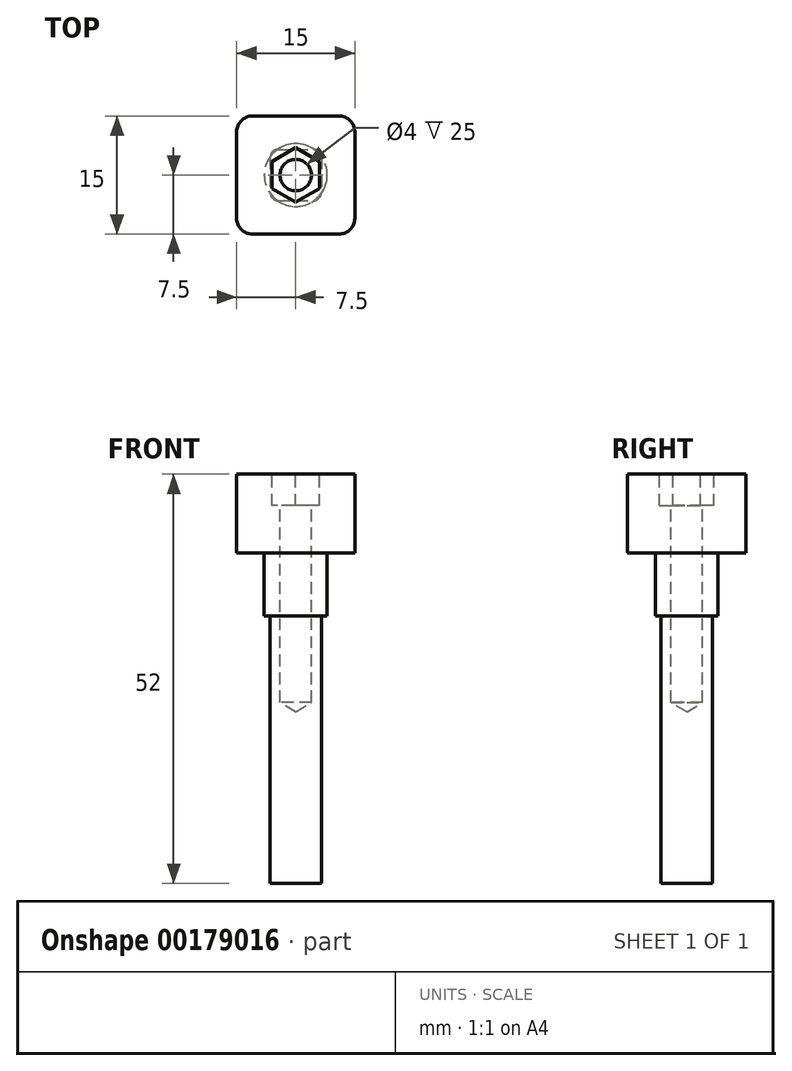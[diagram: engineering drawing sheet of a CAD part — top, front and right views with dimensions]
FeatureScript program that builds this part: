
annotation { "Feature Type Name" : "Feature", "Feature Type Description" : "" }
export const myFeature = defineFeature(function(context is Context, id is Id, definition is map)
    precondition{}
    {
        {
            var Q0;
            Q0=qCreatedBy(makeId("Top.planeOp"),FACE);
            var sketch = newSketch(context, id + "F0", { "sketchPlane" : qUnion([Q0])});
            skLineSegment(sketch, "E0.bottom", {"start": v(-3.25, 3.25) * mm, "end": v(3.25, 3.25) * mm});
            skLineSegment(sketch, "E0.top", {"start": v(-3.25, -3.25) * mm, "end": v(3.25, -3.25) * mm});
            skLineSegment(sketch, "E0.left", {"start": v(-3.25, 3.25) * mm, "end": v(-3.25, -3.25) * mm});
            skLineSegment(sketch, "E0.right", {"start": v(3.25, 3.25) * mm, "end": v(3.25, -3.25) * mm});
            skPoint(sketch, "E0.middle", {"position": v(0, 0) * mm});
            skSolve(sketch);
        }
        {
            var Q0;
            Q0 = qSketchRegion(id + "F0", true);
            extrude(context, id + "F1", {"entities" : qUnion([Q0]), "depth" : 34 * mm});
        }
        {
            var Q0;
            Q0=makeQuery(id+"F1.opExtrude","SWEPT_EDGE",EDGE,{"disambiguationData":[OSD([sQuery(id+"F0.wireOp",EDGE,"E0.bottom"),sQuery(id+"F0.wireOp",EDGE,"E0.left")])]});
            var Q1;
            Q1=makeQuery(id+"F1.opExtrude","SWEPT_EDGE",EDGE,{"disambiguationData":[OSD([sQuery(id+"F0.wireOp",EDGE,"E0.bottom"),sQuery(id+"F0.wireOp",EDGE,"E0.right")])]});
            var Q2;
            Q2=makeQuery(id+"F1.opExtrude","SWEPT_EDGE",EDGE,{"disambiguationData":[OSD([sQuery(id+"F0.wireOp",EDGE,"E0.top"),sQuery(id+"F0.wireOp",EDGE,"E0.right")])]});
            var Q3;
            Q3=makeQuery(id+"F1.opExtrude","SWEPT_EDGE",EDGE,{"disambiguationData":[OSD([sQuery(id+"F0.wireOp",EDGE,"E0.top"),sQuery(id+"F0.wireOp",EDGE,"E0.left")])]});
            fillet(context, id + "F2", {"entities" : qUnion([Q0, Q1, Q2, Q3]), "radius" : 1 * mm, "tangentPropagation" : true, "allowEdgeOverflow" : false});
        }
        {
            var Q0;
            Q0=makeQuery(id+"F1.opExtrude","CAP_FACE",FACE,{"disambiguationData":[OSD([sQuery(id+"F0.wireOp",EDGE,"E0.bottom"),sQuery(id+"F0.wireOp",EDGE,"E0.top"),sQuery(id+"F0.wireOp",EDGE,"E0.left"),sQuery(id+"F0.wireOp",EDGE,"E0.right")])],"isStart":false});
            var sketch = newSketch(context, id + "F3", { "sketchPlane" : qUnion([Q0])});
            skCircle(sketch, "E1", {"center": v(0, 0) * mm, "radius": 4 * mm});
            skSolve(sketch);
        }
        {
            var Q0;
            Q0=makeQuery(id+"F3.imprint","IMPRINT",FACE,{"disambiguationData":[TD([[makeQuery(id+"F3.imprint","IMPRINT",EDGE,{"derivedFrom":sQuery(id+"F3.wireOp",EDGE,"E1")}),1.0]])]});
            var Q1;
            {var subQ3=sQuery(id+"F0.wireOp",EDGE,"E0.bottom");Q1=makeQuery(id+"F3.imprint","IMPRINT",FACE,{"disambiguationData":[TD([[makeQuery(id+"F3.imprint","IMPRINT",EDGE,{"derivedFrom":makeQuery(id+"F1.opExtrude","CAP_EDGE",EDGE,{"disambiguationData":[OSD([subQ3])],"isStart":false})}),-1.0]])]});}
            var Q2;
            {var subQ1=sQuery(id+"F0.wireOp",EDGE,"E0.right");var subQ9=makeQuery(id+"F1.opExtrude","CAP_EDGE",EDGE,{"disambiguationData":[OSD([subQ1])],"isStart":false});Q2=makeQuery(id+"F3.imprint","IMPRINT",FACE,{"disambiguationData":[TD([[makeQuery(id+"F3.imprint","IMPRINT",EDGE,{"derivedFrom":subQ9}),1.0]])]});}
            var Q3;
            {var subQ3=sQuery(id+"F0.wireOp",EDGE,"E0.bottom");var subQ9=makeQuery(id+"F1.opExtrude","CAP_EDGE",EDGE,{"disambiguationData":[OSD([subQ3])],"isStart":false});Q3=makeQuery(id+"F3.imprint","IMPRINT",FACE,{"disambiguationData":[TD([[makeQuery(id+"F3.imprint","IMPRINT",EDGE,{"derivedFrom":subQ9}),1.0]])]});}
            var Q4;
            {var subQ3=sQuery(id+"F0.wireOp",EDGE,"E0.top");var subQ9=makeQuery(id+"F1.opExtrude","CAP_EDGE",EDGE,{"disambiguationData":[OSD([subQ3])],"isStart":false});Q4=makeQuery(id+"F3.imprint","IMPRINT",FACE,{"disambiguationData":[TD([[makeQuery(id+"F3.imprint","IMPRINT",EDGE,{"derivedFrom":subQ9}),-1.0]])]});}
            var Q5;
            {var subQ1=sQuery(id+"F0.wireOp",EDGE,"E0.left");var subQ9=makeQuery(id+"F1.opExtrude","CAP_EDGE",EDGE,{"disambiguationData":[OSD([subQ1])],"isStart":false});Q5=makeQuery(id+"F3.imprint","IMPRINT",FACE,{"disambiguationData":[TD([[makeQuery(id+"F3.imprint","IMPRINT",EDGE,{"derivedFrom":subQ9}),-1.0]])]});}
            extrude(context, id + "F4", {"entities" : qUnion([Q0, Q1, Q2, Q3, Q4, Q5]), "operationType" : NewBodyOperationType.ADD, "depth" : 8 * mm});
        }
        {
            var Q0;
            Q0=makeQuery(id+"F4.opExtrude","CAP_FACE",FACE,{"disambiguationData":[OSD([sQuery(id+"F3.wireOp",EDGE,"E1")])],"isStart":false});
            var sketch = newSketch(context, id + "F5", { "sketchPlane" : qUnion([Q0])});
            skLineSegment(sketch, "E2.bottom", {"start": v(-7.5, 7.5) * mm, "end": v(7.5, 7.5) * mm});
            skLineSegment(sketch, "E2.top", {"start": v(-7.5, -7.5) * mm, "end": v(7.5, -7.5) * mm});
            skLineSegment(sketch, "E2.left", {"start": v(-7.5, 7.5) * mm, "end": v(-7.5, -7.5) * mm});
            skLineSegment(sketch, "E2.right", {"start": v(7.5, 7.5) * mm, "end": v(7.5, -7.5) * mm});
            skPoint(sketch, "E2.middle", {"position": v(0, 0) * mm});
            skSolve(sketch);
        }
        {
            var Q0;
            Q0=makeQuery(id+"F5.imprint","IMPRINT",FACE,{"disambiguationData":[TD([[makeQuery(id+"F5.imprint","IMPRINT",EDGE,{"derivedFrom":sQuery(id+"F5.wireOp",EDGE,"E2.bottom")}),-1.0]])]});
            var Q1;
            Q1=makeQuery(id+"F5.imprint","IMPRINT",FACE,{"disambiguationData":[TD([[makeQuery(id+"F5.imprint","IMPRINT",EDGE,{"derivedFrom":makeQuery(id+"F4.opExtrude","CAP_EDGE",EDGE,{"disambiguationData":[OSD([sQuery(id+"F3.wireOp",EDGE,"E1")])],"isStart":false})}),1.0]])]});
            extrude(context, id + "F6", {"entities" : qUnion([Q0, Q1]), "operationType" : NewBodyOperationType.ADD, "depth" : 10 * mm});
        }
        {
            var Q0;
            Q0=makeQuery(id+"F6.opExtrude","CAP_FACE",FACE,{"disambiguationData":[OSD([sQuery(id+"F5.wireOp",EDGE,"E2.bottom"),sQuery(id+"F5.wireOp",EDGE,"E2.top"),sQuery(id+"F5.wireOp",EDGE,"E2.left"),sQuery(id+"F5.wireOp",EDGE,"E2.right")])],"isStart":false});
            var sketch = newSketch(context, id + "F7", { "sketchPlane" : qUnion([Q0])});
            skCircle(sketch, "E3.cCircle", {"center": v(0, 0) * mm, "radius": 3 * mm, "construction": true});
            skLineSegment(sketch, "E3.0", {"start": v(-3, -1.73) * mm, "end": v(-3, 1.73) * mm});
            skLineSegment(sketch, "E3.1", {"start": v(-3, 1.73) * mm, "end": v(0, 3.46) * mm});
            skLineSegment(sketch, "E3.2", {"start": v(0, 3.46) * mm, "end": v(3, 1.73) * mm});
            skLineSegment(sketch, "E3.3", {"start": v(3, 1.73) * mm, "end": v(3, -1.73) * mm});
            skLineSegment(sketch, "E3.4", {"start": v(3, -1.73) * mm, "end": v(0, -3.46) * mm});
            skLineSegment(sketch, "E3.5", {"start": v(0, -3.46) * mm, "end": v(-3, -1.73) * mm});
            skPoint(sketch, "E3.0.midPoint", {"position": v(-3, 0) * mm});
            skSolve(sketch);
        }
        {
            var Q0;
            Q0=makeQuery(id+"F7.imprint","IMPRINT",FACE,{"disambiguationData":[TD([[makeQuery(id+"F7.imprint","IMPRINT",EDGE,{"derivedFrom":sQuery(id+"F7.wireOp",EDGE,"E3.0")}),-1.0]])]});
            extrude(context, id + "F8", {"entities" : qUnion([Q0]), "operationType" : NewBodyOperationType.REMOVE, "oppositeDirection" : true, "depth" : 4 * mm});
        }
        {
            var Q0;
            Q0=makeQuery(id+"F8.boolean.opBoolean","COPY",FACE,{"derivedFrom":makeQuery(id+"F8.opExtrude","CAP_FACE",FACE,{"disambiguationData":[OSD([sQuery(id+"F7.wireOp",EDGE,"E3.0"),sQuery(id+"F7.wireOp",EDGE,"E3.1"),sQuery(id+"F7.wireOp",EDGE,"E3.2"),sQuery(id+"F7.wireOp",EDGE,"E3.3"),sQuery(id+"F7.wireOp",EDGE,"E3.4"),sQuery(id+"F7.wireOp",EDGE,"E3.5")])],"isStart":false})});
            var sketch = newSketch(context, id + "F9", { "sketchPlane" : qUnion([Q0])});
            skPoint(sketch, "E4", {"position": v(0, 0) * mm});
            skSolve(sketch);
        }
        {
            var Q0;
            Q0=sQuery(id+"F9.wireOp",VERTEX,"E4");
            var Q1;
            Q1=makeQuery(id+"F1.opExtrude","SWEPT_BODY",BODY,{"disambiguationData":[OSD([sQuery(id+"F0.wireOp",EDGE,"E0.bottom"),sQuery(id+"F0.wireOp",EDGE,"E0.top"),sQuery(id+"F0.wireOp",EDGE,"E0.left"),sQuery(id+"F0.wireOp",EDGE,"E0.right")])]});
            hole(context, id + "F10", {"style" : HoleStyle.SIMPLE, "endStyle" : HoleEndStyle.BLIND, "holeDiameter" : 4 * mm, "holeDepth" : 25 * mm, "locations" : qUnion([Q0]), "scope" : qUnion([Q1])});
        }
        {
            var Q0;
            Q0=makeQuery(id+"F6.opExtrude","SWEPT_EDGE",EDGE,{"disambiguationData":[OSD([sQuery(id+"F5.wireOp",EDGE,"E2.bottom"),sQuery(id+"F5.wireOp",EDGE,"E2.right")])]});
            var Q1;
            Q1=makeQuery(id+"F6.opExtrude","SWEPT_EDGE",EDGE,{"disambiguationData":[OSD([sQuery(id+"F5.wireOp",EDGE,"E2.bottom"),sQuery(id+"F5.wireOp",EDGE,"E2.left")])]});
            var Q2;
            Q2=makeQuery(id+"F6.opExtrude","SWEPT_EDGE",EDGE,{"disambiguationData":[OSD([sQuery(id+"F5.wireOp",EDGE,"E2.top"),sQuery(id+"F5.wireOp",EDGE,"E2.left")])]});
            var Q3;
            Q3=makeQuery(id+"F6.opExtrude","SWEPT_EDGE",EDGE,{"disambiguationData":[OSD([sQuery(id+"F5.wireOp",EDGE,"E2.top"),sQuery(id+"F5.wireOp",EDGE,"E2.right")])]});
            fillet(context, id + "F11", {"entities" : qUnion([Q0, Q1, Q2, Q3]), "radius" : 2 * mm, "tangentPropagation" : true, "allowEdgeOverflow" : false});
        }
    });
